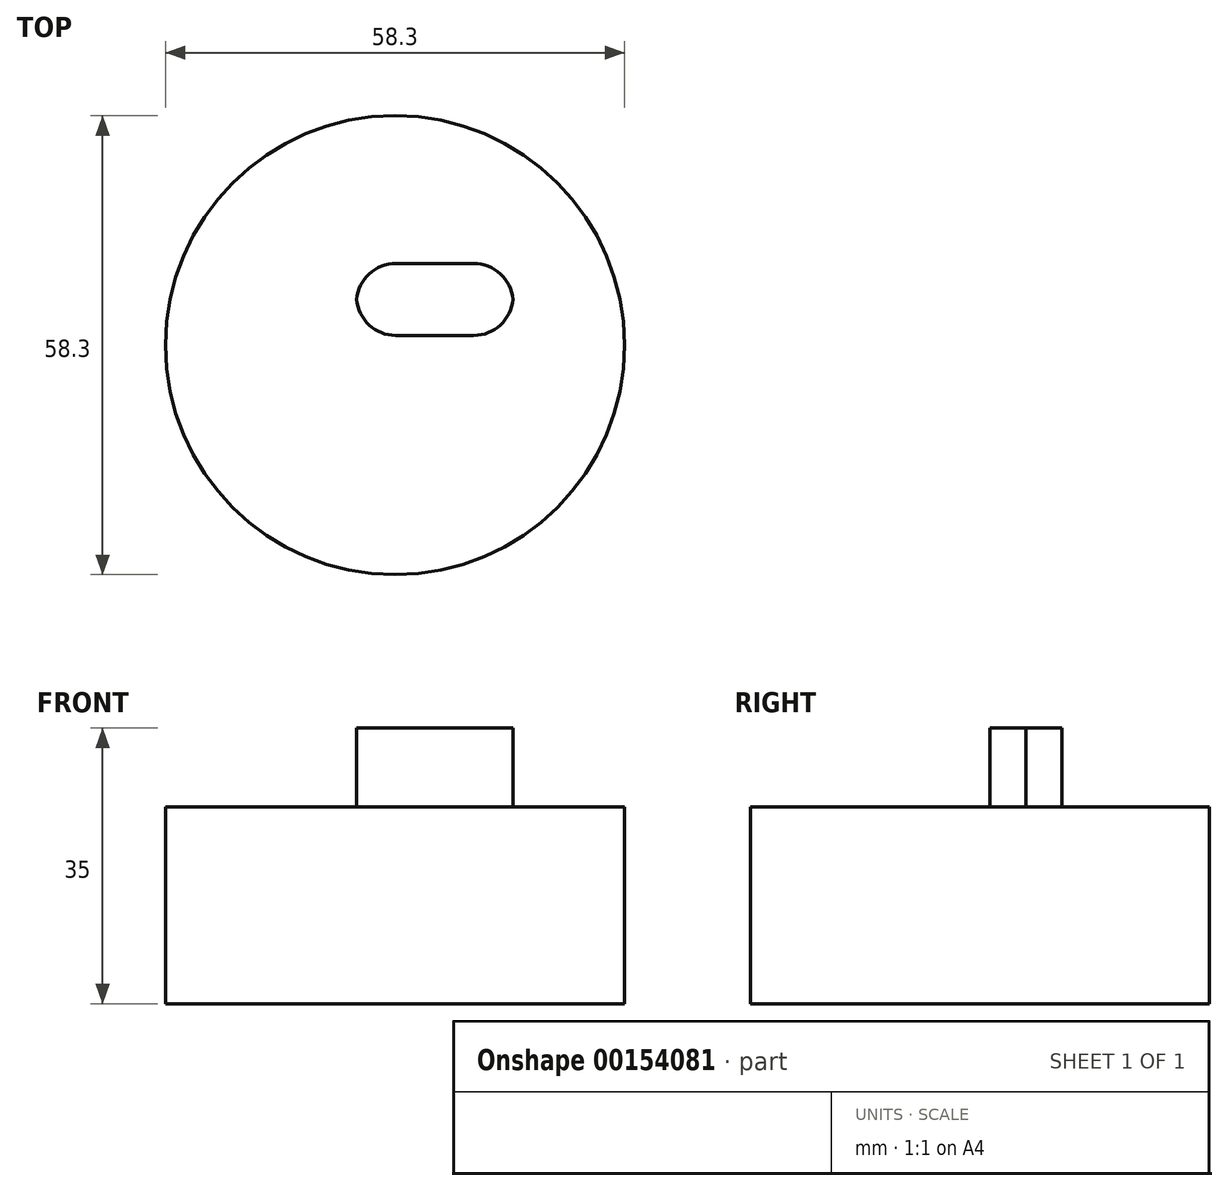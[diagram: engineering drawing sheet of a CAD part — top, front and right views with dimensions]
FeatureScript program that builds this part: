
annotation { "Feature Type Name" : "Feature", "Feature Type Description" : "" }
export const myFeature = defineFeature(function(context is Context, id is Id, definition is map)
    precondition{}
    {
        {
            var Q0;
            Q0=qCreatedBy(makeId("Top.planeOp"),FACE);
            var sketch = newSketch(context, id + "F0", { "sketchPlane" : qUnion([Q0])});
            skCircle(sketch, "E0", {"center": v(-25, 15) * mm, "radius": 29.15 * mm});
            skSolve(sketch);
        }
        {
            var Q0;
            Q0 = qSketchRegion(id + "F0", true);
            extrude(context, id + "F1", {"entities" : qUnion([Q0]), "depth" : 25 * mm});
        }
        {
            var Q0;
            Q0=makeQuery(id+"F1.opExtrude","CAP_FACE",FACE,{"disambiguationData":[OSD([sQuery(id+"F0.wireOp",EDGE,"E0")])],"isStart":false});
            var sketch = newSketch(context, id + "F2", { "sketchPlane" : qUnion([Q0])});
            skLineSegment(sketch, "E1.bottom", {"start": v(-29.9, 25.38) * mm, "end": v(-10, 25.38) * mm});
            skLineSegment(sketch, "E1.top", {"start": v(-29.9, 16.25) * mm, "end": v(-10, 16.25) * mm});
            skLineSegment(sketch, "E1.left", {"start": v(-29.9, 25.38) * mm, "end": v(-29.9, 16.25) * mm});
            skLineSegment(sketch, "E1.right", {"start": v(-10, 25.38) * mm, "end": v(-10, 16.25) * mm});
            skSolve(sketch);
        }
        {
            var Q0;
            Q0=makeQuery(id+"F2.imprint","IMPRINT",FACE,{"disambiguationData":[TD([[makeQuery(id+"F2.imprint","IMPRINT",EDGE,{"derivedFrom":sQuery(id+"F2.wireOp",EDGE,"E1.bottom")}),-1.0]])]});
            extrude(context, id + "F3", {"entities" : qUnion([Q0]), "operationType" : NewBodyOperationType.ADD, "depth" : 10 * mm});
        }
        {
            var Q0;
            Q0=makeQuery(id+"F3.opExtrude","SWEPT_EDGE",EDGE,{"disambiguationData":[OSD([sQuery(id+"F2.wireOp",EDGE,"E1.top"),sQuery(id+"F2.wireOp",EDGE,"E1.left")])]});
            var Q1;
            Q1=makeQuery(id+"F3.opExtrude","SWEPT_EDGE",EDGE,{"disambiguationData":[OSD([sQuery(id+"F2.wireOp",EDGE,"E1.top"),sQuery(id+"F2.wireOp",EDGE,"E1.right")])]});
            var Q2;
            Q2=makeQuery(id+"F3.opExtrude","SWEPT_EDGE",EDGE,{"disambiguationData":[OSD([sQuery(id+"F2.wireOp",EDGE,"E1.bottom"),sQuery(id+"F2.wireOp",EDGE,"E1.left")])]});
            var Q3;
            Q3=makeQuery(id+"F3.opExtrude","SWEPT_EDGE",EDGE,{"disambiguationData":[OSD([sQuery(id+"F2.wireOp",EDGE,"E1.bottom"),sQuery(id+"F2.wireOp",EDGE,"E1.right")])]});
            fillet(context, id + "F4", {"entities" : qUnion([Q0, Q1, Q2, Q3]), "radius" : 5 * mm, "tangentPropagation" : true, "allowEdgeOverflow" : false});
        }
    });
